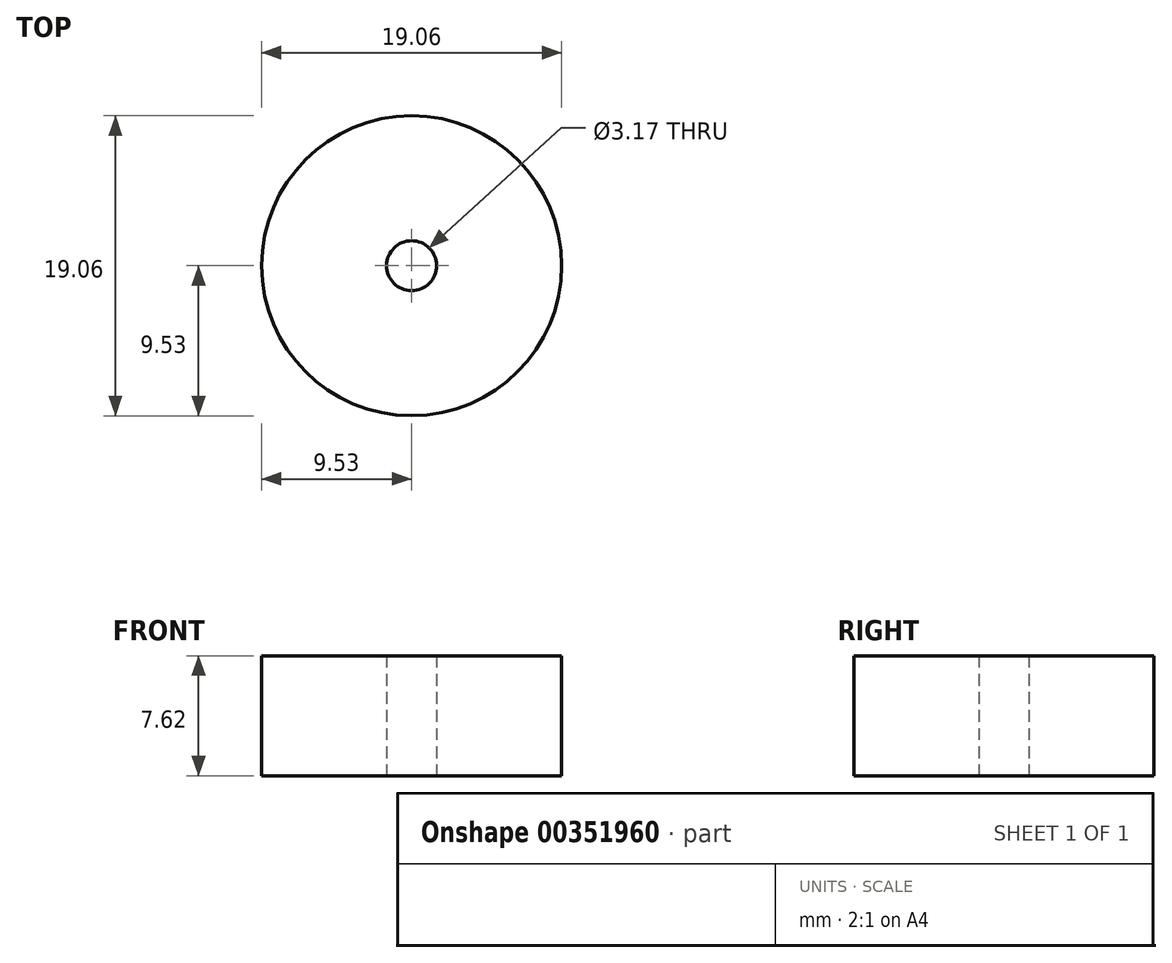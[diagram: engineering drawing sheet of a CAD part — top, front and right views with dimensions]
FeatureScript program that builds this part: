
annotation { "Feature Type Name" : "Feature", "Feature Type Description" : "" }
export const myFeature = defineFeature(function(context is Context, id is Id, definition is map)
    precondition{}
    {
        {
            var Q0;
            Q0=qCreatedBy(makeId("Top.planeOp"),FACE);
            var sketch = newSketch(context, id + "F0", { "sketchPlane" : qUnion([Q0])});
            skCircle(sketch, "E0", {"center": v(0, 0) * mm, "radius": 9.53 * mm});
            skCircle(sketch, "E1", {"center": v(0, 0) * mm, "radius": 1.59 * mm});
            skSolve(sketch);
        }
        {
            var Q0;
            Q0 = qSketchRegion(id + "F0", true);
            extrude(context, id + "F1", {"entities" : qUnion([Q0]), "depth" : 7.62 * mm});
        }
        {
            var Q0;
            Q0=sQuery(id+"F0.wireOp",EDGE,"E0");
            extrude(context, id + "F2", {"bodyType" : ToolBodyType.SURFACE, "surfaceEntities" : qUnion([Q0]), "depth" : 7.62 * mm});
        }
    });
